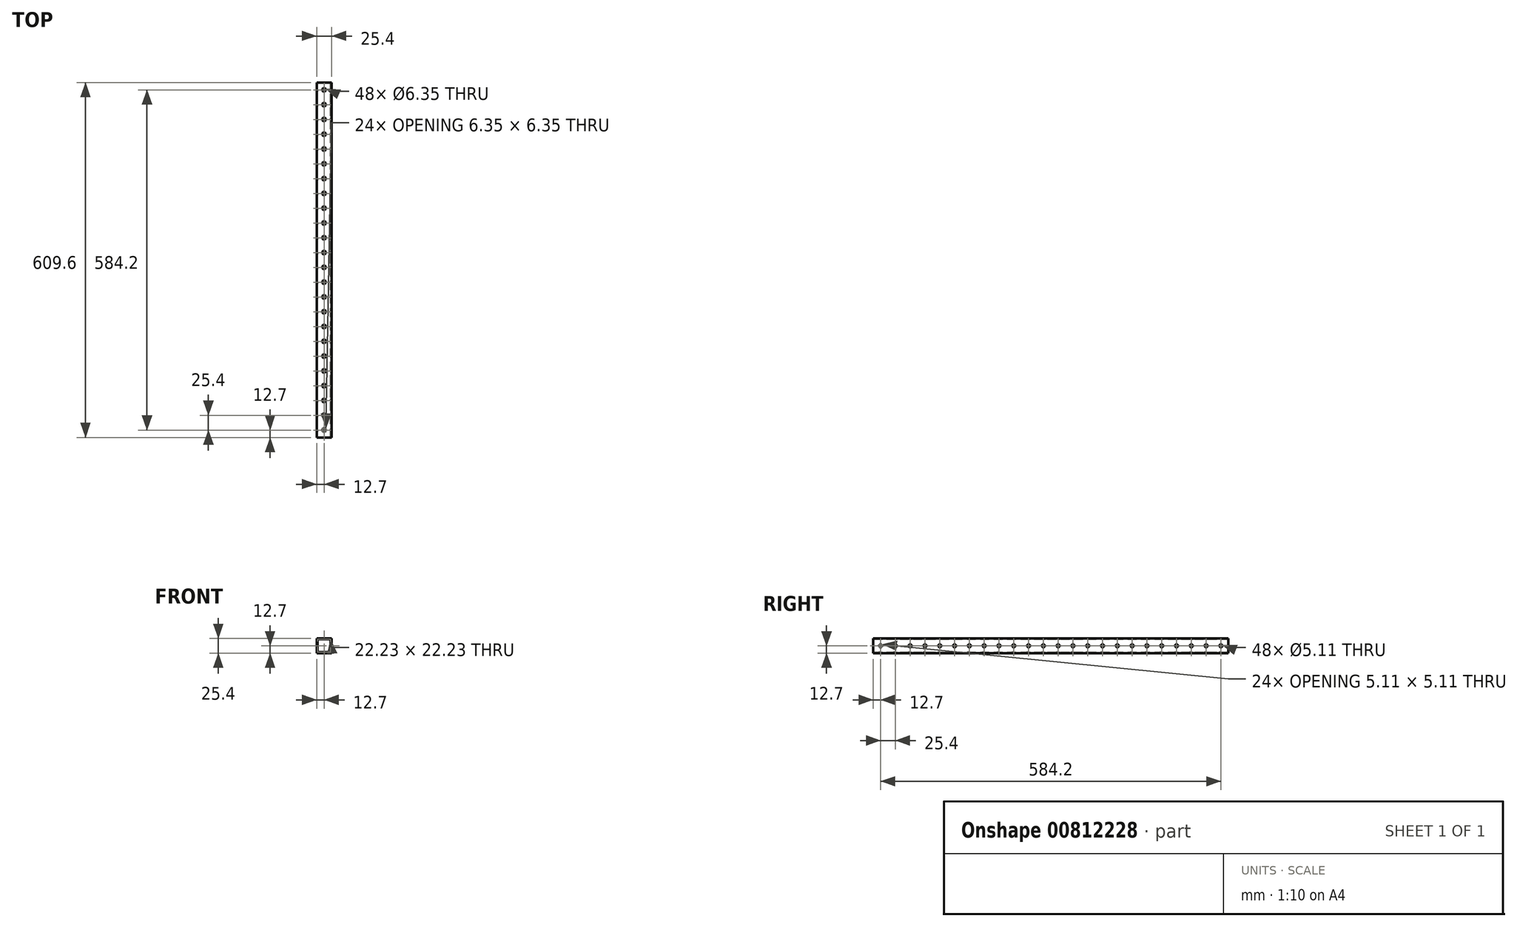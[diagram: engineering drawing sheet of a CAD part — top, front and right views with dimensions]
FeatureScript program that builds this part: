
annotation { "Feature Type Name" : "Feature", "Feature Type Description" : "" }
export const myFeature = defineFeature(function(context is Context, id is Id, definition is map)
    precondition{}
    {
        {
            var Q0;
            Q0=qCreatedBy(makeId("Front.planeOp"),FACE);
            var sketch = newSketch(context, id + "F0", { "sketchPlane" : qUnion([Q0])});
            skLineSegment(sketch, "E0.bottom", {"start": v(12.7, 12.7) * mm, "end": v(-12.7, 12.7) * mm});
            skLineSegment(sketch, "E0.top", {"start": v(12.7, -12.7) * mm, "end": v(-12.7, -12.7) * mm});
            skLineSegment(sketch, "E0.left", {"start": v(12.7, 12.7) * mm, "end": v(12.7, -12.7) * mm});
            skLineSegment(sketch, "E0.right", {"start": v(-12.7, 12.7) * mm, "end": v(-12.7, -12.7) * mm});
            skPoint(sketch, "E0.middle", {"position": v(0, 0) * mm});
            skLineSegment(sketch, "E1.0", {"start": v(11.11, -11.11) * mm, "end": v(-11.11, -11.11) * mm});
            skLineSegment(sketch, "E1.1", {"start": v(11.11, 11.11) * mm, "end": v(11.11, -11.11) * mm});
            skLineSegment(sketch, "E1.2", {"start": v(11.11, 11.11) * mm, "end": v(-11.11, 11.11) * mm});
            skLineSegment(sketch, "E1.3", {"start": v(-11.11, 11.11) * mm, "end": v(-11.11, -11.11) * mm});
            skSolve(sketch);
        }
        {
            var Q0;
            Q0 = qSketchRegion(id + "F0", true);
            extrude(context, id + "F1", {"entities" : qUnion([Q0]), "depth" : 609.6 * mm, "offsetDistance" : 25.4 * mm});
        }
        {
            var Q0;
            Q0=makeQuery(id+"F1.opExtrude","SWEPT_FACE",FACE,{"disambiguationData":[OSD([sQuery(id+"F0.wireOp",EDGE,"E0.bottom")])]});
            var sketch = newSketch(context, id + "F2", { "sketchPlane" : qUnion([Q0])});
            skCircle(sketch, "E2", {"center": v(0, -12.7) * mm, "radius": 3.18 * mm});
            skCircle(sketch, "E3.0.1.0", {"center": v(0, -38.1) * mm, "radius": 3.18 * mm});
            skCircle(sketch, "E3.0.2.0", {"center": v(0, -63.5) * mm, "radius": 3.18 * mm});
            skCircle(sketch, "E3.0.3.0", {"center": v(0, -88.9) * mm, "radius": 3.18 * mm});
            skCircle(sketch, "E3.0.4.0", {"center": v(0, -114.3) * mm, "radius": 3.18 * mm});
            skCircle(sketch, "E3.0.5.0", {"center": v(0, -139.7) * mm, "radius": 3.18 * mm});
            skCircle(sketch, "E3.0.6.0", {"center": v(0, -165.1) * mm, "radius": 3.18 * mm});
            skCircle(sketch, "E3.0.7.0", {"center": v(0, -190.5) * mm, "radius": 3.18 * mm});
            skCircle(sketch, "E3.0.8.0", {"center": v(0, -215.9) * mm, "radius": 3.18 * mm});
            skCircle(sketch, "E3.0.9.0", {"center": v(0, -241.3) * mm, "radius": 3.18 * mm});
            skCircle(sketch, "E3.0.10.0", {"center": v(0, -266.7) * mm, "radius": 3.18 * mm});
            skCircle(sketch, "E3.0.11.0", {"center": v(0, -292.1) * mm, "radius": 3.18 * mm});
            skCircle(sketch, "E3.0.12.0", {"center": v(0, -317.5) * mm, "radius": 3.18 * mm});
            skCircle(sketch, "E3.0.13.0", {"center": v(0, -342.9) * mm, "radius": 3.18 * mm});
            skCircle(sketch, "E3.0.14.0", {"center": v(0, -368.3) * mm, "radius": 3.18 * mm});
            skCircle(sketch, "E3.0.15.0", {"center": v(0, -393.7) * mm, "radius": 3.18 * mm});
            skCircle(sketch, "E3.0.16.0", {"center": v(0, -419.1) * mm, "radius": 3.18 * mm});
            skCircle(sketch, "E3.0.17.0", {"center": v(0, -444.5) * mm, "radius": 3.18 * mm});
            skCircle(sketch, "E3.0.18.0", {"center": v(0, -469.9) * mm, "radius": 3.18 * mm});
            skCircle(sketch, "E3.0.19.0", {"center": v(0, -495.3) * mm, "radius": 3.18 * mm});
            skCircle(sketch, "E3.0.20.0", {"center": v(0, -520.7) * mm, "radius": 3.18 * mm});
            skCircle(sketch, "E3.0.21.0", {"center": v(0, -546.1) * mm, "radius": 3.18 * mm});
            skCircle(sketch, "E3.0.22.0", {"center": v(0, -571.5) * mm, "radius": 3.18 * mm});
            skCircle(sketch, "E3.0.23.0", {"center": v(0, -596.9) * mm, "radius": 3.18 * mm});
            skLineSegment(sketch, "E3.direction1", {"start": v(0, -12.7) * mm, "end": v(25.4, -12.7) * mm, "construction": true});
            skLineSegment(sketch, "E3.direction2", {"start": v(0, -12.7) * mm, "end": v(0, -38.1) * mm, "construction": true});
            skSolve(sketch);
        }
        {
            var Q0;
            Q0 = qSketchRegion(id + "F2", true);
            extrude(context, id + "F3", {"entities" : qUnion([Q0]), "operationType" : NewBodyOperationType.REMOVE, "oppositeDirection" : true, "depth" : 25.4 * mm, "offsetDistance" : 25.4 * mm});
        }
        {
            var Q0;
            Q0=makeQuery(id+"F1.opExtrude","SWEPT_FACE",FACE,{"disambiguationData":[OSD([sQuery(id+"F0.wireOp",EDGE,"E0.right")])]});
            var sketch = newSketch(context, id + "F4", { "sketchPlane" : qUnion([Q0])});
            skCircle(sketch, "E4", {"center": v(12.7, 0) * mm, "radius": 2.55 * mm});
            skCircle(sketch, "E5.1.0.0", {"center": v(38.1, 0) * mm, "radius": 2.55 * mm});
            skCircle(sketch, "E5.2.0.0", {"center": v(63.5, 0) * mm, "radius": 2.55 * mm});
            skCircle(sketch, "E5.3.0.0", {"center": v(88.9, 0) * mm, "radius": 2.55 * mm});
            skCircle(sketch, "E5.4.0.0", {"center": v(114.3, 0) * mm, "radius": 2.55 * mm});
            skCircle(sketch, "E5.5.0.0", {"center": v(139.7, 0) * mm, "radius": 2.55 * mm});
            skCircle(sketch, "E5.6.0.0", {"center": v(165.1, 0) * mm, "radius": 2.55 * mm});
            skCircle(sketch, "E5.7.0.0", {"center": v(190.5, 0) * mm, "radius": 2.55 * mm});
            skCircle(sketch, "E5.8.0.0", {"center": v(215.9, 0) * mm, "radius": 2.55 * mm});
            skCircle(sketch, "E5.9.0.0", {"center": v(241.3, 0) * mm, "radius": 2.55 * mm});
            skCircle(sketch, "E5.10.0.0", {"center": v(266.7, 0) * mm, "radius": 2.55 * mm});
            skCircle(sketch, "E5.11.0.0", {"center": v(292.1, 0) * mm, "radius": 2.55 * mm});
            skCircle(sketch, "E5.12.0.0", {"center": v(317.5, 0) * mm, "radius": 2.55 * mm});
            skCircle(sketch, "E5.13.0.0", {"center": v(342.9, 0) * mm, "radius": 2.55 * mm});
            skCircle(sketch, "E5.14.0.0", {"center": v(368.3, 0) * mm, "radius": 2.55 * mm});
            skCircle(sketch, "E5.15.0.0", {"center": v(393.7, 0) * mm, "radius": 2.55 * mm});
            skCircle(sketch, "E5.16.0.0", {"center": v(419.1, 0) * mm, "radius": 2.55 * mm});
            skCircle(sketch, "E5.17.0.0", {"center": v(444.5, 0) * mm, "radius": 2.55 * mm});
            skCircle(sketch, "E5.18.0.0", {"center": v(469.9, 0) * mm, "radius": 2.55 * mm});
            skCircle(sketch, "E5.19.0.0", {"center": v(495.3, 0) * mm, "radius": 2.55 * mm});
            skCircle(sketch, "E5.20.0.0", {"center": v(520.7, 0) * mm, "radius": 2.55 * mm});
            skCircle(sketch, "E5.21.0.0", {"center": v(546.1, 0) * mm, "radius": 2.55 * mm});
            skCircle(sketch, "E5.22.0.0", {"center": v(571.5, 0) * mm, "radius": 2.55 * mm});
            skCircle(sketch, "E5.23.0.0", {"center": v(596.9, 0) * mm, "radius": 2.55 * mm});
            skLineSegment(sketch, "E5.direction1", {"start": v(12.7, 0) * mm, "end": v(38.1, 0) * mm, "construction": true});
            skSolve(sketch);
        }
        {
            var Q0;
            Q0 = qSketchRegion(id + "F4", true);
            extrude(context, id + "F5", {"entities" : qUnion([Q0]), "operationType" : NewBodyOperationType.REMOVE, "oppositeDirection" : true, "depth" : 25.4 * mm, "offsetDistance" : 25.4 * mm});
        }
    });
